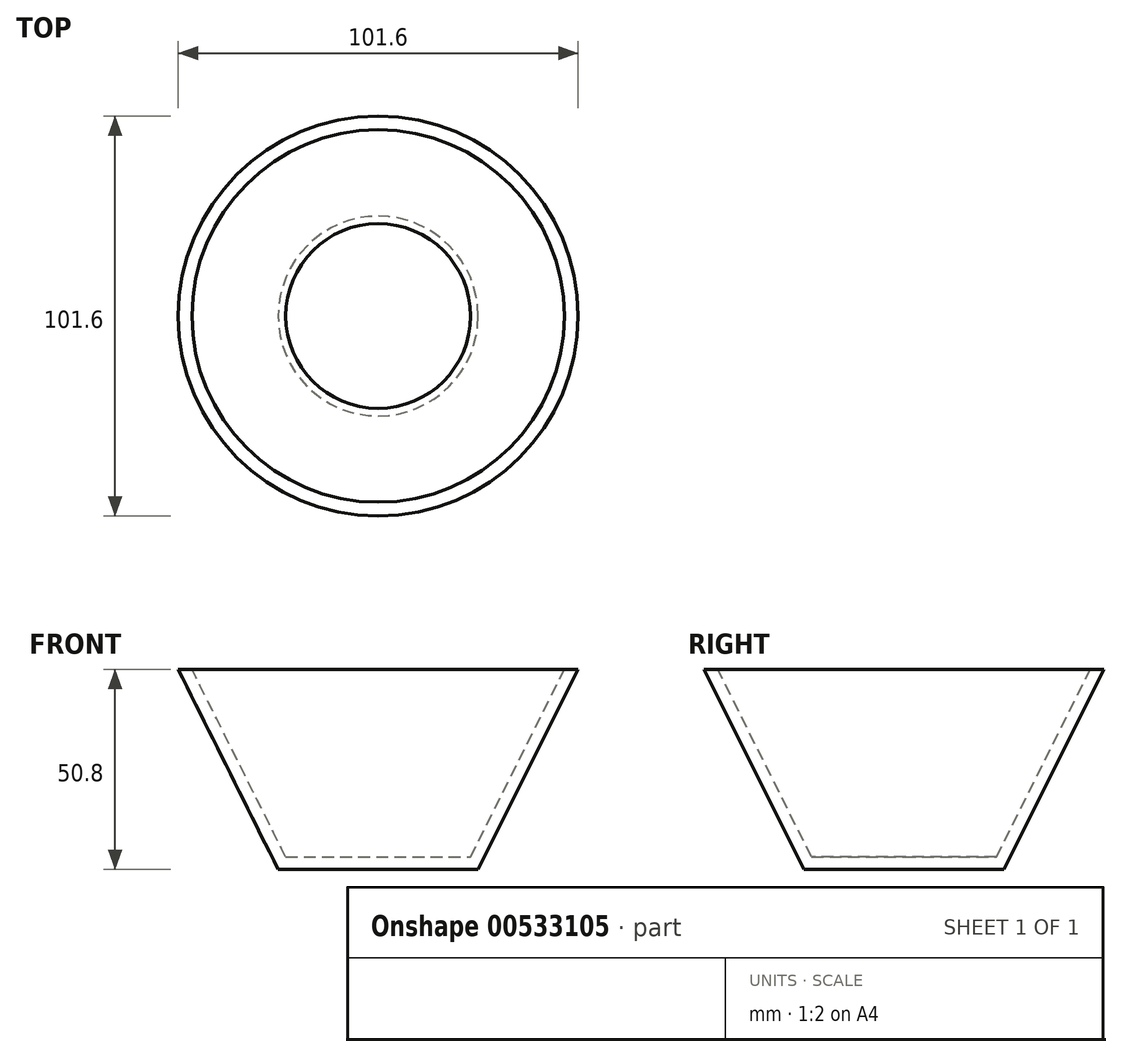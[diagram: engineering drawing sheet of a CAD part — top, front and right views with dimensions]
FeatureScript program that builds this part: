
annotation { "Feature Type Name" : "Feature", "Feature Type Description" : "" }
export const myFeature = defineFeature(function(context is Context, id is Id, definition is map)
    precondition{}
    {
        {
            var Q0;
            Q0=qCreatedBy(makeId("Front.planeOp"),FACE);
            var sketch = newSketch(context, id + "F0", { "sketchPlane" : qUnion([Q0])});
            skLineSegment(sketch, "E0", {"start": v(0, 0) * mm, "end": v(0, 50.8) * mm, "construction": true});
            skLineSegment(sketch, "E1", {"start": v(0, 0) * mm, "end": v(25.4, 0) * mm});
            skLineSegment(sketch, "E2", {"start": v(25.4, 0) * mm, "end": v(50.8, 50.8) * mm});
            skLineSegment(sketch, "E3.0", {"start": v(23.47, 3.12) * mm, "end": v(47.3, 50.8) * mm});
            skLineSegment(sketch, "E3.1", {"start": v(0, 3.12) * mm, "end": v(23.47, 3.12) * mm});
            skLineSegment(sketch, "E4", {"start": v(47.3, 50.8) * mm, "end": v(50.8, 50.8) * mm});
            skLineSegment(sketch, "E5", {"start": v(0, 3.12) * mm, "end": v(0, 0) * mm});
            skSolve(sketch);
        }
        {
            var Q0;
            Q0=makeQuery(id+"F0.imprint","IMPRINT",FACE,{"disambiguationData":[TD([[makeQuery(id+"F0.imprint","IMPRINT",EDGE,{"derivedFrom":sQuery(id+"F0.wireOp",EDGE,"E1")}),1.0]])]});
            var Q1;
            Q1=sQuery(id+"F0.wireOp",EDGE,"E0");
            revolve(context, id + "F1", {"entities" : qUnion([Q0]), "axis" : qUnion([Q1]), "revolveType" : RevolveType.FULL});
        }
    });
